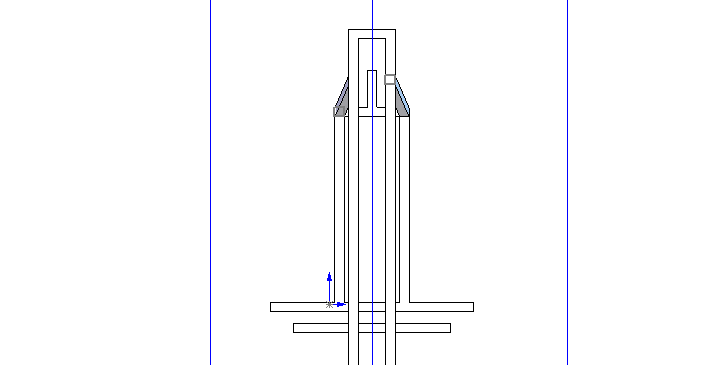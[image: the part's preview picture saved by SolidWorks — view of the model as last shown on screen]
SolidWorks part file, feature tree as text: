
SOLIDWORKS PART (.sldprt)
format: sldprt  version: not decoded by parser v0  size: 341,504 bytes
history: native  units: mm
features: sketch x10, extrude x4, plane x4, sweep x2, mirror x1 (+11 scaffold rows collapsed)
feature tree (32):
  scaffold x11  (default folders/planes/origin — collapsed)
  sketch  "Sketch2"  dims[D1=558.8mm D2=25.4mm D3=406.4mm D4=152.4mm D5=76.2mm D6=101.6mm D7=12.7mm D8=25.4mm D9=25.4mm D10=25.4mm D11=25.4mm D12=508.0mm]
  extrude  "Extrude1"  Depth=25.4mm
  plane  "Plane1"  Offset=355.6mm
  plane  "Plane2"
  plane  "Plane3"  Offset=355.6mm
  sketch  "Sketch3"  dims[D1=127.0mm D2=63.5mm D3=1168.4mm D4=101.6mm D5=25.4mm]
  extrude  "Extrude2"  Depth=25.4mm
  sketch  "Sketch8"
  plane  "Plane4"  Offset=38.1mm
  sketch  "Sketch14"  dims[D1=25.4mm D2=50.8mm]
  sketch  "3DSketch1"
  sweep  "Sweep1"
  sketch  "Sketch15"  dims[D1=25.4mm D2=25.4mm D3=254.0mm]
  extrude  "Extrude6"  Depth=152.4mm
  sketch  "Sketch16"
  extrude  "Extrude7"  [1 undecoded]
  mirror  "Mirror2"
  sketch  "Sketch17"
  sketch  "Sketch18"
  sketch  "3DSketch3"
  sweep  "Sweep2"
decode coverage: 7 of 17 modeling features carry decoded parameters
note: 1 parameter value undecoded
note: suppression state not decoded; provenance and decode notes live in map.json
